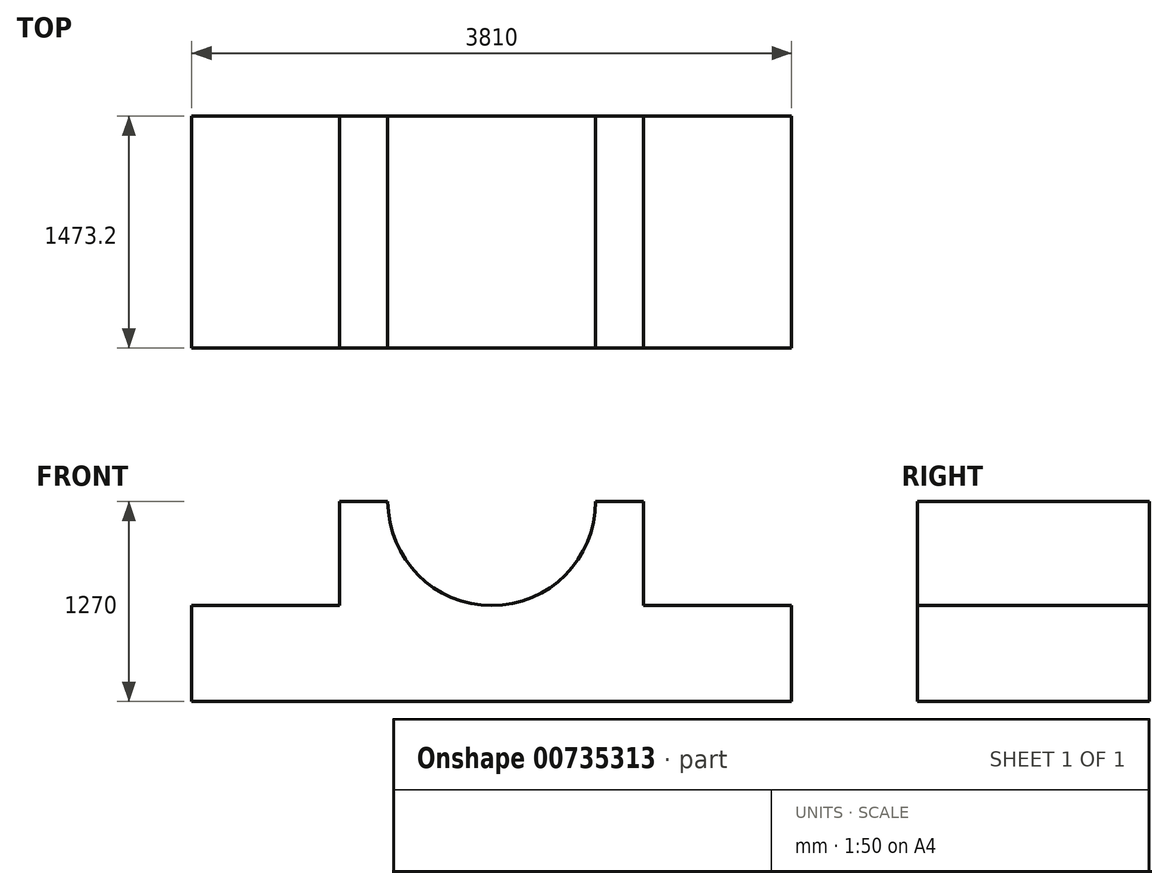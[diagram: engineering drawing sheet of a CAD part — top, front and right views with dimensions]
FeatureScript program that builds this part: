
annotation { "Feature Type Name" : "Feature", "Feature Type Description" : "" }
export const myFeature = defineFeature(function(context is Context, id is Id, definition is map)
    precondition{}
    {
        {
            var Q0;
            Q0=qCreatedBy(makeId("Front.planeOp"),FACE);
            var sketch = newSketch(context, id + "F0", { "sketchPlane" : qUnion([Q0])});
            skLineSegment(sketch, "E0.left", {"start": v(-2017.06, -562.24) * mm, "end": v(-2017.06, -1222.64) * mm});
            skLineSegment(sketch, "E0.right", {"start": v(-86.66, -562.24) * mm, "end": v(-86.66, -1222.64) * mm});
            skLineSegment(sketch, "E1", {"start": v(-86.66, -1222.64) * mm, "end": v(853.14, -1222.64) * mm});
            skLineSegment(sketch, "E2", {"start": v(-2017.06, -1222.64) * mm, "end": v(-2956.86, -1222.64) * mm});
            skLineSegment(sketch, "E3", {"start": v(-2956.86, -1222.64) * mm, "end": v(-2956.86, -1832.24) * mm});
            skLineSegment(sketch, "E4", {"start": v(853.14, -1222.64) * mm, "end": v(853.14, -1832.24) * mm});
            skLineSegment(sketch, "E5", {"start": v(-2956.86, -1832.24) * mm, "end": v(853.14, -1832.24) * mm});
            skLineSegment(sketch, "E6", {"start": v(-2017.06, -562.24) * mm, "end": v(-1712.26, -562.24) * mm});
            skCircle(sketch, "E7", {"center": v(-1051.86, -562.24) * mm, "radius": 660.4 * mm});
            skLineSegment(sketch, "E8", {"start": v(-86.66, -562.24) * mm, "end": v(-391.46, -562.24) * mm});
            skSolve(sketch);
        }
        {
            var Q0;
            Q0=makeQuery(id+"F0.imprint","IMPRINT",FACE,{"disambiguationData":[TD([[makeQuery(id+"F0.imprint","IMPRINT",EDGE,{"derivedFrom":sQuery(id+"F0.wireOp",EDGE,"E0.left")}),1.0]])]});
            extrude(context, id + "F1", {"entities" : qUnion([Q0]), "depth" : 1473.2 * mm, "offsetDistance" : 25.4 * mm});
        }
    });
